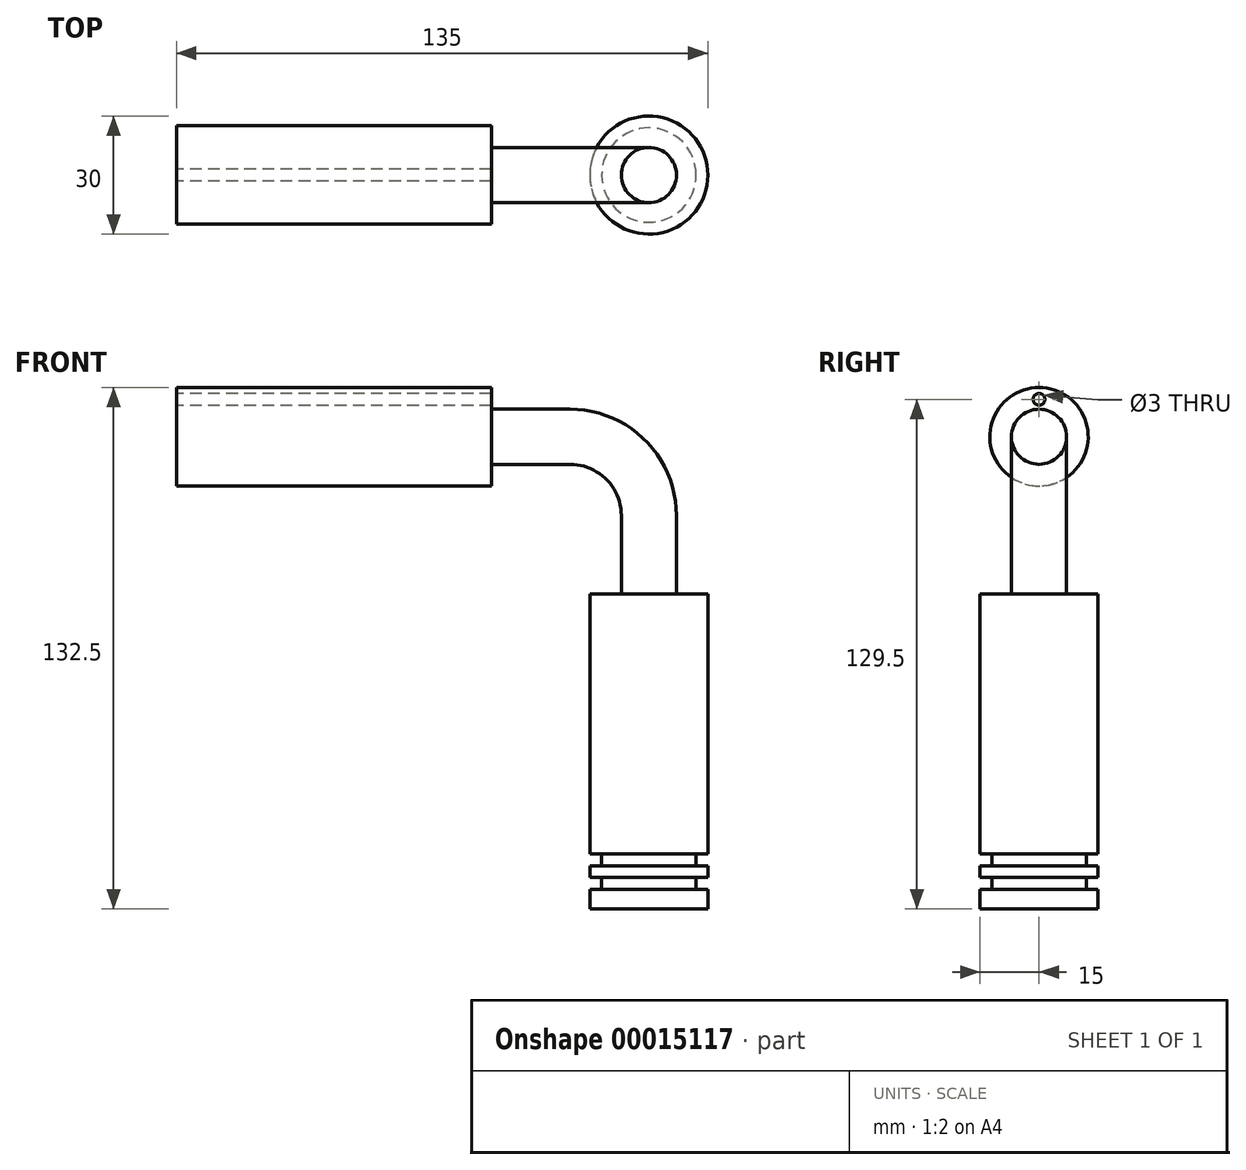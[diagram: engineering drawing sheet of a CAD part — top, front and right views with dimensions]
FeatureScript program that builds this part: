
annotation { "Feature Type Name" : "Feature", "Feature Type Description" : "" }
export const myFeature = defineFeature(function(context is Context, id is Id, definition is map)
    precondition{}
    {
        {
            var Q0;
            Q0=qCreatedBy(makeId("Front.planeOp"),FACE);
            var sketch = newSketch(context, id + "F0", { "sketchPlane" : qUnion([Q0])});
            skLineSegment(sketch, "E0.bottom", {"start": v(0, 0) * mm, "end": v(15, 0) * mm});
            skLineSegment(sketch, "E0.top", {"start": v(0, 80) * mm, "end": v(15, 80) * mm});
            skLineSegment(sketch, "E0.left", {"start": v(0, 0) * mm, "end": v(0, 80) * mm});
            skLineSegment(sketch, "E0.right", {"start": v(15, 0) * mm, "end": v(15, 5) * mm});
            skLineSegment(sketch, "E1", {"start": v(0, 80) * mm, "end": v(0, 100) * mm});
            skLineSegment(sketch, "E2", {"start": v(-20, 120) * mm, "end": v(-40, 120) * mm});
            skLineSegment(sketch, "E3", {"start": v(-40, 120) * mm, "end": v(-40, 107.5) * mm});
            skLineSegment(sketch, "E4", {"start": v(-40, 107.5) * mm, "end": v(-120, 107.5) * mm});
            skLineSegment(sketch, "E5", {"start": v(-120, 107.5) * mm, "end": v(-120, 120) * mm});
            skLineSegment(sketch, "E6", {"start": v(-120, 120) * mm, "end": v(-40, 120) * mm});
            skPoint(sketch, "E7.visualSharp", {"position": v(0, 120) * mm});
            skArc(sketch, "E7.filletArc", {"start": v(0, 100) * mm, "mid": v(-5.86, 114.14) * mm, "end": v(-20, 120) * mm});
            skLineSegment(sketch, "E8.0.MirrorCS", {"start": v(-40, 132.5) * mm, "end": v(-120, 132.5) * mm});
            skLineSegment(sketch, "E9.0.MirrorCS", {"start": v(-40, 120) * mm, "end": v(-40, 132.5) * mm});
            skLineSegment(sketch, "E10.0.MirrorCS", {"start": v(-120, 132.5) * mm, "end": v(-120, 120) * mm});
            skLineSegment(sketch, "E11.0.MirrorCS", {"start": v(-15, 0) * mm, "end": v(-15, 80) * mm});
            skLineSegment(sketch, "E12.0.MirrorCS", {"start": v(0, 0) * mm, "end": v(-15, 0) * mm});
            skLineSegment(sketch, "E13.0.MirrorCS", {"start": v(0, 80) * mm, "end": v(-15, 80) * mm});
            skLineSegment(sketch, "E14.bottom", {"start": v(15, 5) * mm, "end": v(12, 5) * mm});
            skLineSegment(sketch, "E14.top", {"start": v(15, 8) * mm, "end": v(12, 8) * mm});
            skLineSegment(sketch, "E14.right", {"start": v(12, 5) * mm, "end": v(12, 8) * mm});
            skLineSegment(sketch, "E15.bottom", {"start": v(15, 11) * mm, "end": v(12, 11) * mm});
            skLineSegment(sketch, "E15.top", {"start": v(15, 14) * mm, "end": v(12, 14) * mm});
            skLineSegment(sketch, "E15.right", {"start": v(12, 11) * mm, "end": v(12, 14) * mm});
            skLineSegment(sketch, "E16.trimOffspring", {"start": v(15, 8) * mm, "end": v(15, 11) * mm});
            skLineSegment(sketch, "E17.trimOffspring", {"start": v(15, 14) * mm, "end": v(15, 80) * mm});
            skSolve(sketch);
        }
        {
            var Q0;
            Q0=makeQuery(id+"F0.imprint","IMPRINT",FACE,{"disambiguationData":[TD([[makeQuery(id+"F0.imprint","IMPRINT",EDGE,{"derivedFrom":sQuery(id+"F0.wireOp",EDGE,"E0.bottom")}),1.0]])]});
            var Q1;
            Q1=sQuery(id+"F0.wireOp",EDGE,"E1");
            revolve(context, id + "F1", {"entities" : qUnion([Q0]), "axis" : qUnion([Q1]), "revolveType" : RevolveType.FULL});
        }
        {
            var Q0;
            Q0=makeQuery(id+"F0.imprint","IMPRINT",FACE,{"disambiguationData":[TD([[makeQuery(id+"F0.imprint","IMPRINT",EDGE,{"derivedFrom":sQuery(id+"F0.wireOp",EDGE,"E6")}),1.0]])]});
            var Q1;
            Q1=sQuery(id+"F0.wireOp",EDGE,"E6");
            revolve(context, id + "F2", {"entities" : qUnion([Q0]), "axis" : qUnion([Q1]), "revolveType" : RevolveType.FULL});
        }
        {
            var Q0;
            Q0=makeQuery(id+"F2.opRevolve","SWEPT_FACE",FACE,{"disambiguationData":[OSD([sQuery(id+"F0.wireOp",EDGE,"E10.0.MirrorCS")])]});
            var sketch = newSketch(context, id + "F3", { "sketchPlane" : qUnion([Q0])});
            skCircle(sketch, "E18.0", {"center": v(0, 120) * mm, "radius": 12.5 * mm});
            skCircle(sketch, "E19", {"center": v(0, 129.5) * mm, "radius": 1.5 * mm});
            skSolve(sketch);
        }
        {
            var Q0;
            Q0=makeQuery(id+"F3.imprint","IMPRINT",FACE,{"disambiguationData":[TD([[makeQuery(id+"F3.imprint","IMPRINT",EDGE,{"derivedFrom":sQuery(id+"F3.wireOp",EDGE,"E19")}),1.0]])]});
            extrude(context, id + "F4", {"entities" : qUnion([Q0]), "operationType" : NewBodyOperationType.REMOVE, "endBound" : BoundingType.THROUGH_ALL, "oppositeDirection" : true, "depth" : 25 * mm});
        }
        {
            var Q0;
            Q0=makeQuery(id+"F1.opRevolve","SWEPT_FACE",FACE,{"disambiguationData":[OSD([sQuery(id+"F0.wireOp",EDGE,"E0.top")])]});
            var sketch = newSketch(context, id + "F5", { "sketchPlane" : qUnion([Q0])});
            skCircle(sketch, "E20.0", {"center": v(0, 0) * mm, "radius": 15 * mm});
            skCircle(sketch, "E21", {"center": v(0, 0) * mm, "radius": 7 * mm});
            skSolve(sketch);
        }
        {
            var Q0;
            Q0=makeQuery(id+"F5.imprint","IMPRINT",FACE,{"disambiguationData":[TD([[makeQuery(id+"F5.imprint","IMPRINT",EDGE,{"derivedFrom":sQuery(id+"F5.wireOp",EDGE,"E21")}),1.0]])]});
            var Q1;
            Q1=sQuery(id+"F0.wireOp",EDGE,"E1");
            var Q2;
            Q2=sQuery(id+"F0.wireOp",EDGE,"E7.filletArc");
            var Q3;
            Q3=sQuery(id+"F0.wireOp",EDGE,"E2");
            sweep(context, id + "F6", {"operationType" : NewBodyOperationType.ADD, "profiles" : qUnion([Q0]), "path" : qUnion([Q1, Q2, Q3])});
        }
    });
